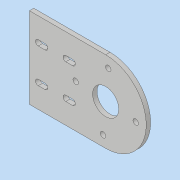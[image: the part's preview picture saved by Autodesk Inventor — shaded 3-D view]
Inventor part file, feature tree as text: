
AUTODESK INVENTOR PART (.ipt)
format: ipt  version: 2017 (Build 210142000, 142)  size: 142,848 bytes
history: native  units: in
note: dims shown in document units (in); Inventor stores cm internally (conversion verified against a paired STEP export)
features: sketch x1, extrude x1
ambient origin geometry x8: Origin, YZ Plane, XZ Plane, XY Plane, X Axis, Y Axis, Z Axis, Center Point
bodies: Solid1 (feature_tree)
feature tree (2):
  sketch  "Sketch1"  dims[d0=2.3228in d1=2.185in d2=0.75in d3=0.1575in d4=0.1575in d5=0.1575in d6=0.1575in d7=2.4393in d8=1.2205in d9=1.2205in d10=1.2205in d11=2.6394in d13=0.159in d14=0.159in d16=0.159in d17=0.159in d18=0.159in d19=0.159in d20=0.159in d21=0.159in d22=0.1969in d23=0.1969in d24=0.1969in d25=0.1969in d26=0.159in d27=0.7874in d29=0.7874in d30=0.125in d31=0.0in d32=0.9843in]
  extrude  "Extrusion1"  Depth=0.9843in
